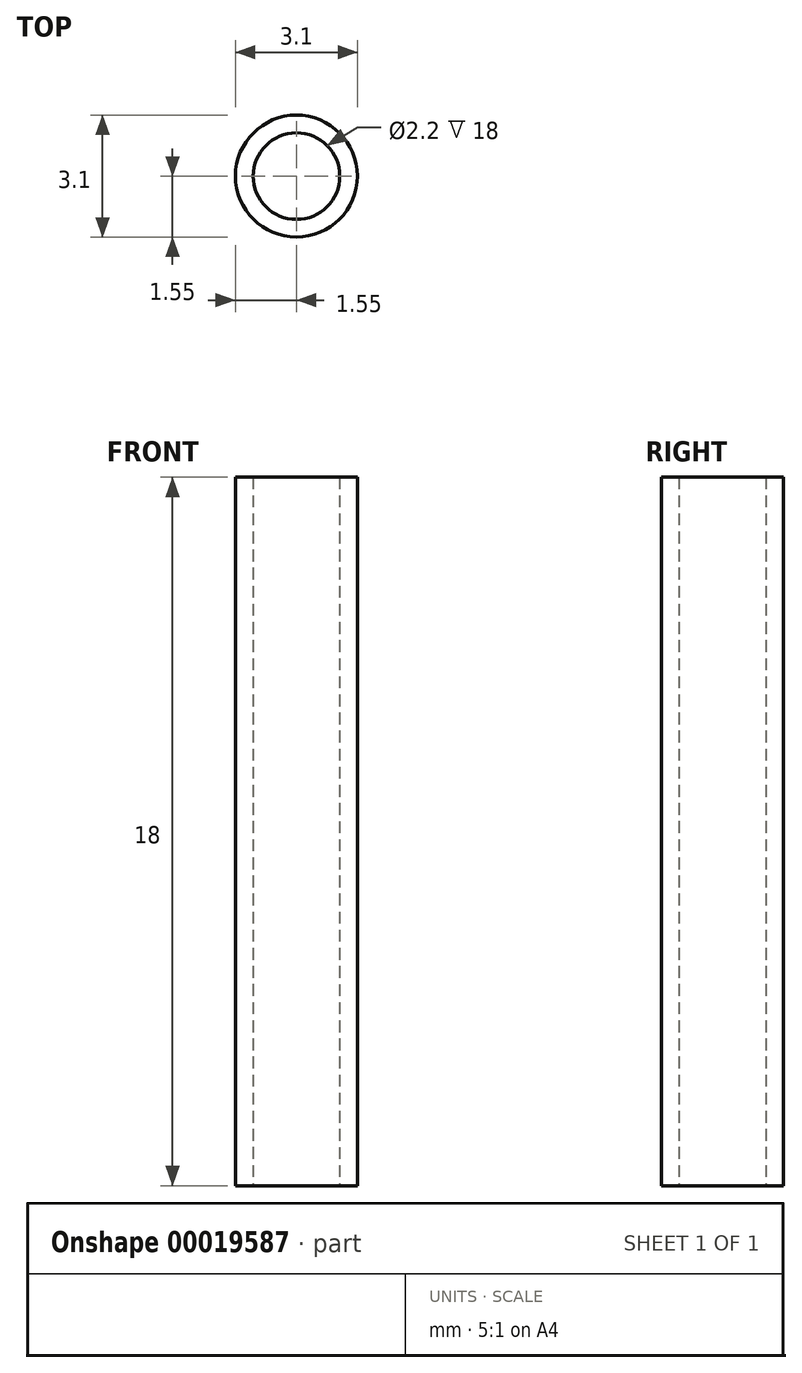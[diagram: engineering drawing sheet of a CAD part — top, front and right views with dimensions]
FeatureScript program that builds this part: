
annotation { "Feature Type Name" : "Feature", "Feature Type Description" : "" }
export const myFeature = defineFeature(function(context is Context, id is Id, definition is map)
    precondition{}
    {
        {
            var Q0;
            Q0=qCreatedBy(makeId("Top.planeOp"),FACE);
            var sketch = newSketch(context, id + "F0", { "sketchPlane" : qUnion([Q0])});
            skCircle(sketch, "E0", {"center": v(0, 0) * mm, "radius": 1.55 * mm});
            skCircle(sketch, "E1", {"center": v(0, 0) * mm, "radius": 1.1 * mm});
            skSolve(sketch);
        }
        {
            var Q0;
            Q0=qSketchRegion(id+"F0",true);
            extrude(context, id + "F1", {"entities" : qUnion([Q0]), "depth" : 18 * mm});
        }
    });
